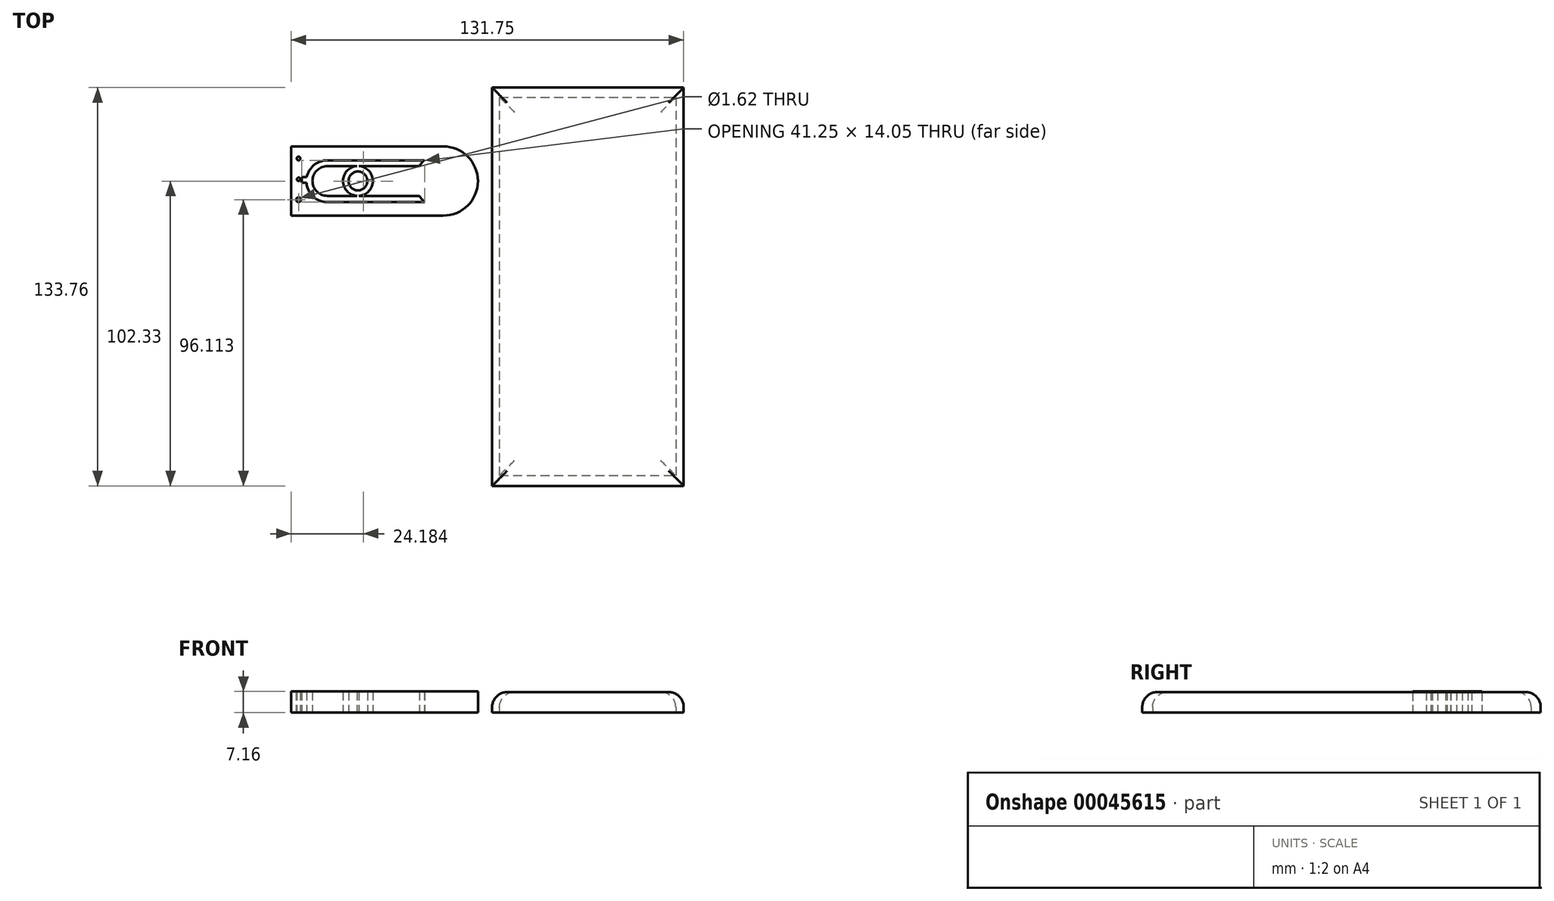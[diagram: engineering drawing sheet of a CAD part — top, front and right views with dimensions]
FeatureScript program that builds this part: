
annotation { "Feature Type Name" : "Feature", "Feature Type Description" : "" }
export const myFeature = defineFeature(function(context is Context, id is Id, definition is map)
    precondition{}
    {
        {
            var Q0;
            Q0=qCreatedBy(makeId("Top.planeOp"),FACE);
            var sketch = newSketch(context, id + "F0", { "sketchPlane" : qUnion([Q0])});
            skLineSegment(sketch, "E0", {"start": v(-13.77, 49.4) * mm, "end": v(-64.81, 49.4) * mm});
            skLineSegment(sketch, "E1", {"start": v(-64.81, 49.4) * mm, "end": v(-64.81, 26.15) * mm});
            skLineSegment(sketch, "E2", {"start": v(-64.81, 26.15) * mm, "end": v(-13.77, 26.15) * mm});
            skArc(sketch, "E3", {"start": v(-13.77, 26.15) * mm, "mid": v(-2.15, 37.77) * mm, "end": v(-13.77, 49.4) * mm});
            skCircle(sketch, "E4", {"center": v(-13.77, 37.77) * mm, "radius": 9.45 * mm});
            skCircle(sketch, "E5", {"center": v(-13.77, 37.77) * mm, "radius": 7.26 * mm});
            skCircle(sketch, "E6", {"center": v(-42.4, 37.77) * mm, "radius": 5 * mm});
            skPoint(sketch, "E6.centerSnap0", {"position": v(-64.81, 37.77) * mm});
            skCircle(sketch, "E7", {"center": v(-42.4, 37.77) * mm, "radius": 3.17 * mm});
            skLineSegment(sketch, "E8", {"start": v(-42.73, 42.76) * mm, "end": v(-21.8, 42.76) * mm});
            skLineSegment(sketch, "E9", {"start": v(-42.73, 32.79) * mm, "end": v(-21.8, 32.79) * mm});
            skLineSegment(sketch, "E10", {"start": v(-42.73, 42.76) * mm, "end": v(-52.67, 42.76) * mm});
            skLineSegment(sketch, "E11", {"start": v(-42.73, 32.79) * mm, "end": v(-52.67, 32.79) * mm});
            skArc(sketch, "E12", {"start": v(-52.67, 42.76) * mm, "mid": v(-57.65, 37.77) * mm, "end": v(-52.67, 32.79) * mm});
            skLineSegment(sketch, "E13", {"start": v(-42.73, 30.67) * mm, "end": v(-20, 30.67) * mm});
            skLineSegment(sketch, "E14", {"start": v(-42.73, 44.73) * mm, "end": v(-20.17, 44.73) * mm});
            skLineSegment(sketch, "E15", {"start": v(-42.73, 44.73) * mm, "end": v(-52.67, 44.73) * mm});
            skLineSegment(sketch, "E16", {"start": v(-42.73, 30.67) * mm, "end": v(-52.67, 30.67) * mm});
            skArc(sketch, "E17", {"start": v(-52.67, 44.73) * mm, "mid": v(-59.7, 37.7) * mm, "end": v(-52.67, 30.67) * mm});
            skLineSegment(sketch, "E18", {"start": v(-63.39, 46.03) * mm, "end": v(-63.39, 30.65) * mm});
            skLineSegment(sketch, "E19", {"start": v(-61.25, 46.03) * mm, "end": v(-61.25, 30.65) * mm});
            skArc(sketch, "E20", {"start": v(-61.25, 46.03) * mm, "mid": v(-62.32, 47.1) * mm, "end": v(-63.39, 46.03) * mm});
            skArc(sketch, "E21", {"start": v(-63.39, 30.65) * mm, "mid": v(-62.32, 29.58) * mm, "end": v(-61.25, 30.65) * mm});
            skLineSegment(sketch, "E22", {"start": v(-61.25, 39.03) * mm, "end": v(-59.57, 39.03) * mm});
            skLineSegment(sketch, "E23", {"start": v(-61.25, 37.23) * mm, "end": v(-59.68, 37.23) * mm});
            skCircle(sketch, "E24", {"center": v(-62.32, 45.33) * mm, "radius": 0.6 * mm});
            skCircle(sketch, "E25", {"center": v(-62.32, 38.34) * mm, "radius": 0.57 * mm});
            skPoint(sketch, "E25.centerSnap0", {"position": v(-61.25, 38.34) * mm});
            skCircle(sketch, "E26", {"center": v(-62.32, 31.48) * mm, "radius": 0.8 * mm});
            skSolve(sketch);
        }
        {
            var Q0;
            Q0=makeQuery(id+"F0.imprint","IMPRINT",FACE,{"disambiguationData":[TD([[makeQuery(id+"F0.imprint","IMPRINT",EDGE,{"derivedFrom":sQuery(id+"F0.wireOp",EDGE,"E5")}),1.0]])]});
            var Q1;
            Q1=makeQuery(id+"F0.imprint","IMPRINT",FACE,{"disambiguationData":[TD([[makeQuery(id+"F0.imprint","IMPRINT",EDGE,{"derivedFrom":sQuery(id+"F0.wireOp",EDGE,"E5")}),-1.0]])]});
            var Q2;
            Q2=makeQuery(id+"F0.imprint","IMPRINT",FACE,{"disambiguationData":[TD([[makeQuery(id+"F0.imprint","IMPRINT",EDGE,{"derivedFrom":sQuery(id+"F0.wireOp",EDGE,"E0")}),1.0]])]});
            var Q3;
            {var subQ3=sQuery(id+"F0.wireOp",EDGE,"E4");var subQ5=sQuery(id+"F0.wireOp",EDGE,"E8");var subQ7=makeQuery(id+"F0.imprint","INTERSECT",VERTEX,{"derivedFrom":[subQ3,subQ5]});Q3=makeQuery(id+"F0.imprint","IMPRINT",FACE,{"disambiguationData":[TD([[makeQuery(id+"F0.imprint","IMPRINT",EDGE,{"disambiguationData":[TD([[subQ7,-1.0]])],"derivedFrom":subQ3}),-1.0]])]});}
            var Q4;
            Q4=makeQuery(id+"F0.imprint","IMPRINT",FACE,{"disambiguationData":[TD([[makeQuery(id+"F0.imprint","IMPRINT",EDGE,{"derivedFrom":sQuery(id+"F0.wireOp",EDGE,"E7")}),1.0]])]});
            var Q5;
            {var subQ1=sQuery(id+"F0.wireOp",EDGE,"E10");Q5=makeQuery(id+"F0.imprint","IMPRINT",FACE,{"disambiguationData":[TD([[makeQuery(id+"F0.imprint","IMPRINT",EDGE,{"derivedFrom":subQ1}),1.0]])]});}
            var Q6;
            Q6=makeQuery(id+"F0.imprint","IMPRINT",FACE,{"disambiguationData":[TD([[makeQuery(id+"F0.imprint","IMPRINT",EDGE,{"derivedFrom":sQuery(id+"F0.wireOp",EDGE,"E18")}),1.0]])]});
            extrude(context, id + "F1", {"entities" : qUnion([Q0, Q1, Q2, Q3, Q4, Q5, Q6]), "depth" : 7.16 * mm});
        }
        {
            var Q0;
            Q0=qCreatedBy(makeId("Top.planeOp"),FACE);
            var sketch = newSketch(context, id + "F2", { "sketchPlane" : qUnion([Q0])});
            skLineSegment(sketch, "E27", {"start": v(33.92, 65.95) * mm, "end": v(33.92, -61.05) * mm});
            skLineSegment(sketch, "E28.bottom", {"start": v(5.08, 65.95) * mm, "end": v(64.28, 65.95) * mm});
            skLineSegment(sketch, "E28.top", {"start": v(5.08, -61.14) * mm, "end": v(64.28, -61.14) * mm});
            skLineSegment(sketch, "E28.left", {"start": v(5.08, 65.95) * mm, "end": v(5.08, -61.14) * mm});
            skLineSegment(sketch, "E28.right", {"start": v(64.28, 65.95) * mm, "end": v(64.28, -61.14) * mm});
            skSolve(sketch);
        }
        {
            var Q0;
            Q0=qCreatedBy(makeId("Top.planeOp"),FACE);
            var sketch = newSketch(context, id + "F3", { "sketchPlane" : qUnion([Q0])});
            skLineSegment(sketch, "E29.bottom", {"start": v(2.62, 69.13) * mm, "end": v(66.94, 69.13) * mm});
            skLineSegment(sketch, "E29.top", {"start": v(2.62, -64.63) * mm, "end": v(66.94, -64.63) * mm});
            skLineSegment(sketch, "E29.left", {"start": v(2.62, 69.13) * mm, "end": v(2.62, -64.63) * mm});
            skLineSegment(sketch, "E29.right", {"start": v(66.94, 69.13) * mm, "end": v(66.94, -64.63) * mm});
            skSolve(sketch);
        }
        {
            var Q0;
            Q0=makeQuery(id+"F2.imprint","IMPRINT",FACE,{"disambiguationData":[TD([[makeQuery(id+"F2.imprint","IMPRINT",EDGE,{"derivedFrom":sQuery(id+"F2.wireOp",EDGE,"E28.top")}),1.0]])]});
            var Q1;
            Q1=makeQuery(id+"F3.imprint","IMPRINT",FACE,{"disambiguationData":[TD([[makeQuery(id+"F3.imprint","IMPRINT",EDGE,{"derivedFrom":sQuery(id+"F3.wireOp",EDGE,"E29.bottom")}),-1.0]])]});
            extrude(context, id + "F4", {"entities" : qUnion([Q0, Q1]), "depth" : 6.9 * mm});
        }
        {
            var Q0;
            Q0=makeQuery(id+"F4.opExtrude","CAP_EDGE",EDGE,{"disambiguationData":[OSD([sQuery(id+"F3.wireOp",EDGE,"E29.bottom")])],"isStart":false});
            var Q1;
            Q1=makeQuery(id+"F4.opExtrude","CAP_EDGE",EDGE,{"disambiguationData":[OSD([sQuery(id+"F3.wireOp",EDGE,"E29.right")])],"isStart":false});
            var Q2;
            Q2=makeQuery(id+"F4.opExtrude","CAP_EDGE",EDGE,{"disambiguationData":[OSD([sQuery(id+"F3.wireOp",EDGE,"E29.left")])],"isStart":false});
            var Q3;
            Q3=makeQuery(id+"F4.opExtrude","CAP_EDGE",EDGE,{"disambiguationData":[OSD([sQuery(id+"F3.wireOp",EDGE,"E29.top")])],"isStart":false});
            var Q4;
            Q4=makeQuery(id+"F4.opExtrude","CAP_EDGE",EDGE,{"disambiguationData":[OSD([sQuery(id+"F2.wireOp",EDGE,"E28.bottom")])],"isStart":false});
            var Q5;
            Q5=makeQuery(id+"F4.opExtrude","CAP_EDGE",EDGE,{"disambiguationData":[OSD([sQuery(id+"F2.wireOp",EDGE,"E28.right")])],"isStart":false});
            var Q6;
            Q6=makeQuery(id+"F4.opExtrude","CAP_FACE",FACE,{"disambiguationData":[OSD([sQuery(id+"F3.wireOp",EDGE,"E29.bottom"),sQuery(id+"F3.wireOp",EDGE,"E29.top"),sQuery(id+"F3.wireOp",EDGE,"E29.left"),sQuery(id+"F3.wireOp",EDGE,"E29.right")])],"isStart":false});
            var Q7;
            Q7=makeQuery(id+"F4.opExtrude","CAP_EDGE",EDGE,{"disambiguationData":[OSD([sQuery(id+"F2.wireOp",EDGE,"E28.top")])],"isStart":false});
            var Q8;
            Q8=makeQuery(id+"F4.opExtrude","CAP_EDGE",EDGE,{"disambiguationData":[OSD([sQuery(id+"F2.wireOp",EDGE,"E28.left")])],"isStart":false});
            fillet(context, id + "F5", {"entities" : qUnion([Q0, Q1, Q2, Q3, Q4, Q5, Q6, Q7, Q8]), "radius" : 5.08 * mm, "tangentPropagation" : true, "allowEdgeOverflow" : false});
        }
    });
